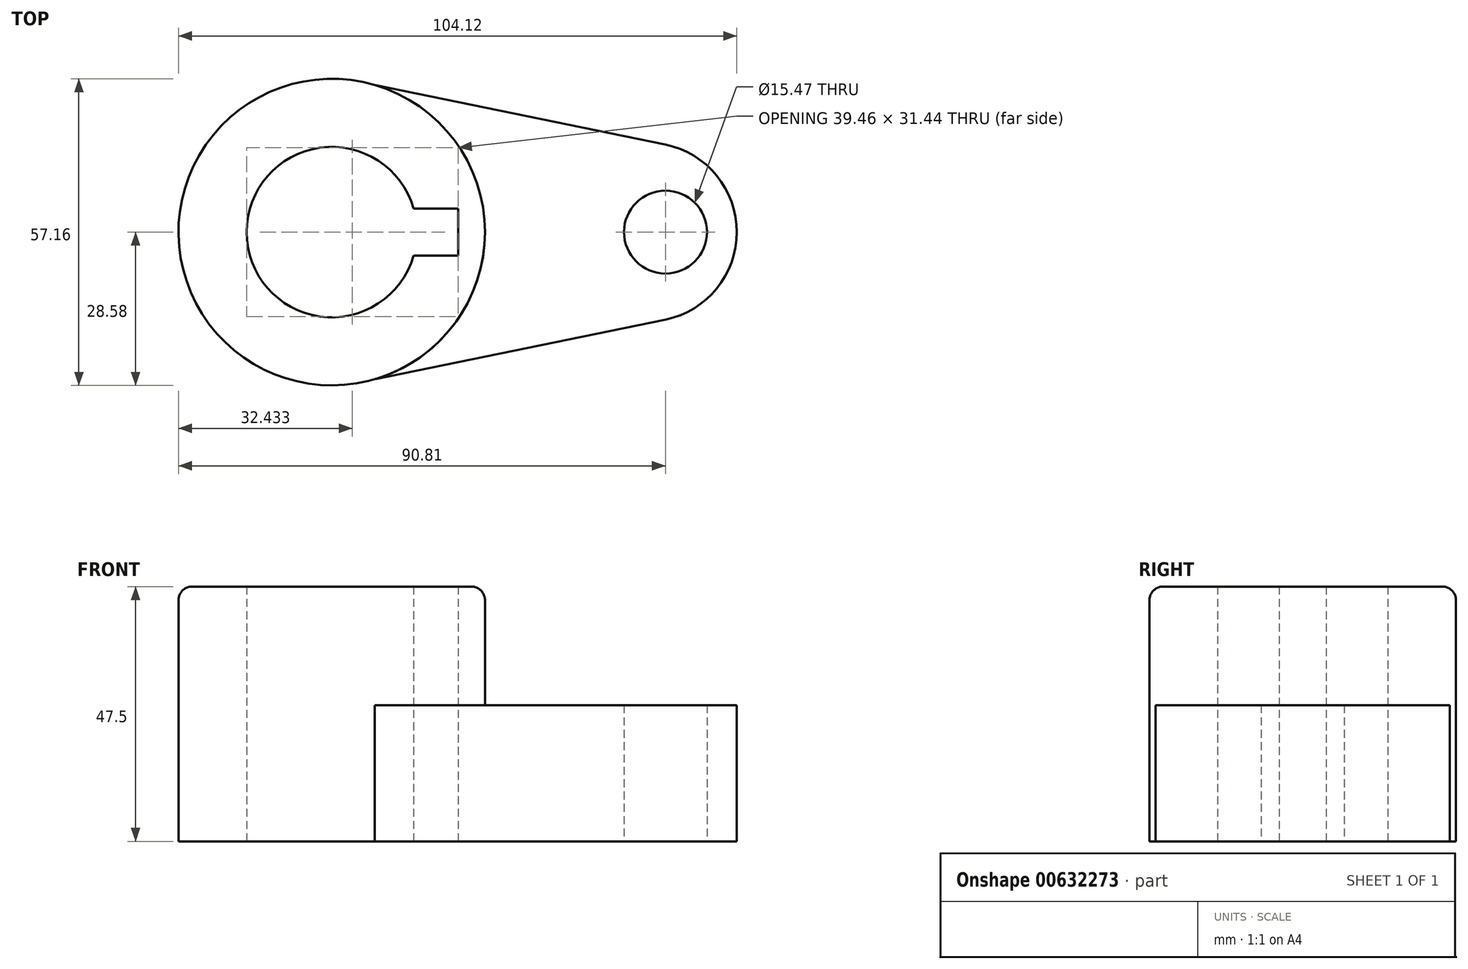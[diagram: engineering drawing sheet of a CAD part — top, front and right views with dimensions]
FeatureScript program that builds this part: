
annotation { "Feature Type Name" : "Feature", "Feature Type Description" : "" }
export const myFeature = defineFeature(function(context is Context, id is Id, definition is map)
    precondition{}
    {
        {
            var Q0;
            Q0=qCreatedBy(makeId("Top.planeOp"),FACE);
            var sketch = newSketch(context, id + "F0", { "sketchPlane" : qUnion([Q0])});
            skCircle(sketch, "E0", {"center": v(0, 0) * mm, "radius": 28.58 * mm});
            skLineSegment(sketch, "E1", {"start": v(0, 0) * mm, "end": v(62.23, 0) * mm});
            skLineSegment(sketch, "E2", {"start": v(8.04, 27.42) * mm, "end": v(62.23, 16.32) * mm});
            skLineSegment(sketch, "E3", {"start": v(8.04, -27.42) * mm, "end": v(62.23, -16.32) * mm});
            skArc(sketch, "E4", {"start": v(62.23, -16.32) * mm, "mid": v(75.54, 0) * mm, "end": v(62.23, 16.32) * mm});
            skCircle(sketch, "E5", {"center": v(62.23, 0) * mm, "radius": 7.73 * mm});
            skCircle(sketch, "E6", {"center": v(0, 0) * mm, "radius": 15.88 * mm});
            skLineSegment(sketch, "E7.bottom", {"start": v(23.58, -4.36) * mm, "end": v(-9.6, -4.36) * mm});
            skLineSegment(sketch, "E7.top", {"start": v(23.58, 4.36) * mm, "end": v(-9.6, 4.36) * mm});
            skLineSegment(sketch, "E7.left", {"start": v(23.58, -4.36) * mm, "end": v(23.58, 4.36) * mm});
            skLineSegment(sketch, "E7.right", {"start": v(-9.6, -4.36) * mm, "end": v(-9.6, 4.36) * mm});
            skPoint(sketch, "E7.middle", {"position": v(6.99, 0) * mm});
            skSolve(sketch);
        }
        {
            var Q0;
            {var subQ0=sQuery(id+"F0.wireOp",EDGE,"E2");Q0=makeQuery(id+"F0.imprint","IMPRINT",FACE,{"disambiguationData":[TD([[makeQuery(id+"F0.imprint","IMPRINT",EDGE,{"derivedFrom":subQ0}),-1.0]])]});}
            extrude(context, id + "F1", {"entities" : qUnion([Q0]), "depth" : 25.4 * mm, "offsetDistance" : 25.4 * mm});
        }
        {
            var Q0;
            {var subQ5=sQuery(id+"F0.wireOp",EDGE,"E0");var subQ7=makeQuery(id+"F0.imprint","IMPRINT",VERTEX,{"derivedFrom":subQ5});Q0=makeQuery(id+"F0.imprint","IMPRINT",FACE,{"disambiguationData":[TD([[makeQuery(id+"F0.imprint","IMPRINT",EDGE,{"disambiguationData":[TD([[subQ7,-1.0]])],"derivedFrom":subQ5}),1.0]])]});}
            extrude(context, id + "F2", {"entities" : qUnion([Q0]), "operationType" : NewBodyOperationType.ADD, "depth" : 47.5 * mm, "offsetDistance" : 25.4 * mm});
        }
        {
            var Q0;
            Q0=makeQuery(id+"F2.opExtrude","CAP_EDGE",EDGE,{"disambiguationData":[OSD([sQuery(id+"F0.wireOp",EDGE,"E0")])],"isStart":false});
            fillet(context, id + "F3", {"entities" : qUnion([Q0]), "radius" : 2.54 * mm, "tangentPropagation" : true, "allowEdgeOverflow" : false});
        }
    });
